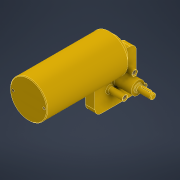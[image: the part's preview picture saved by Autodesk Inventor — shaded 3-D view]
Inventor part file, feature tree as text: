
AUTODESK INVENTOR PART (.ipt)
format: ipt  version: 2021 (Build 250183000, 183)  size: 285,696 bytes
history: native  units: mm
features: sketch x9, extrude x6, plane x5, chamfer x5, thread x3, projected_geometry x2, revolve x1, fillet x1, hole x1, other x1
ambient origin geometry x8: Origin, YZ Plane, XZ Plane, XY Plane, X Axis, Y Axis, Z Axis, Center Point
bodies: Solid1 (feature_tree)
feature tree (34):
  extrude  "Extrusion1"  Depth=139.0mm TaperAngle=0.0deg
  plane  "Work Plane1"
  plane  "Work Plane2"
  sketch  "Sketch2"  dims[d3=62.0mm d4=0.0mm]
  plane  "Work Plane3"
  sketch  "Sketch3"  dims[d5=0.0mm d6=62.0mm]
  extrude  "Extrusion2"  TaperAngle=0.0deg  [1 undecoded]
  revolve  "Revolution1"  [1 undecoded]
  plane  "Work Plane4"
  extrude  "Extrusion3"  Depth=15.0mm TaperAngle=0.0deg
  extrude  "Extrusion4"  Depth=99.5mm
  chamfer  "Chamfer1"  Distance=1.0mm
  fillet  "Fillet1"  Radius=2.0mm
  hole  "Hole1"  [1 undecoded]
  chamfer  "Chamfer3"  Distance=1.0mm
  chamfer  "Chamfer4"  Distance=4.0mm
  plane  "Work Plane5"
  extrude  "Extrusion5"  TaperAngle=0.0deg  [1 undecoded]
  chamfer  "Chamfer5"  Angle=90.0deg  [1 undecoded]
  extrude  "Extrusion6"  Depth=3.0mm
  thread  "Thread1"  [1 undecoded]
  thread  "Thread2"  [1 undecoded]
  thread  "Thread3"  [1 undecoded]
  chamfer  "Chamfer6"  Distance=30.0mm
  other  "calibration32"
  sketch  "Sketch1"  dims[d0=60.0mm d1=139.0mm d2=0.0mm]
  sketch  "Sketch4"  dims[d7=34.6mm d8=15.0mm d9=0.0mm]
  sketch  "Sketch5"  dims[d11=0.0mm d12=99.5mm]
  sketch  "Sketch6"  dims[d13=66.5mm]
  projected_geometry  "Projected Loop1"
  sketch  "Sketch7"  dims[d14=100.6mm]
  sketch  "Sketch8"  dims[d15=4.5mm]
  projected_geometry  "Projected Loop2"
  sketch  "Sketch9"  dims[d16=22.0mm d17=1.0mm d18=2.0mm d19=1.0mm d20=1.0mm d21=4.0mm d22=0.0mm d23=90.0deg d28=3.0mm d29=0.0mm d30=13.0mm d31=4.5mm d32=30.0mm d33=0.0mm d34=1.3mm d35=0.0mm d36=1.0mm d37=2.0mm d38=45.0deg d39=10.0mm d42=0.0mm d43=0.0mm d44=25.0mm d45=25.0mm d46=4.134mm d47=8.0mm d48=4.0mm d49=2.0mm d50=90.0deg d51=8.0mm d52=20.594885mm d56=9.0mm d57=2.0mm d58=45.0deg d59=1.0mm d60=2.0mm d61=45.0deg d62=-5.0mm d64=36.0mm d67=120.0deg d68=120.0deg d69=6.0mm d70=9.0mm d71=6.0mm d72=9.0mm d73=6.0mm d74=9.0mm d75=10.0mm d76=0.0mm d77=2.0mm d78=2.0mm d79=45.0deg d80=6.0mm d81=10.0mm d82=0.0mm d83=25.5mm d84=0.0mm d85=25.5mm d86=0.0mm d87=25.5mm d88=0.0mm d89=1.0mm d90=2.0mm d91=45.0deg d92=32.0mm]
note: 8 required parameter values undecoded (feature->parameter linkage not recoverable at this tier; creation-order binding heuristic only, values carry confidence <= 0.55)